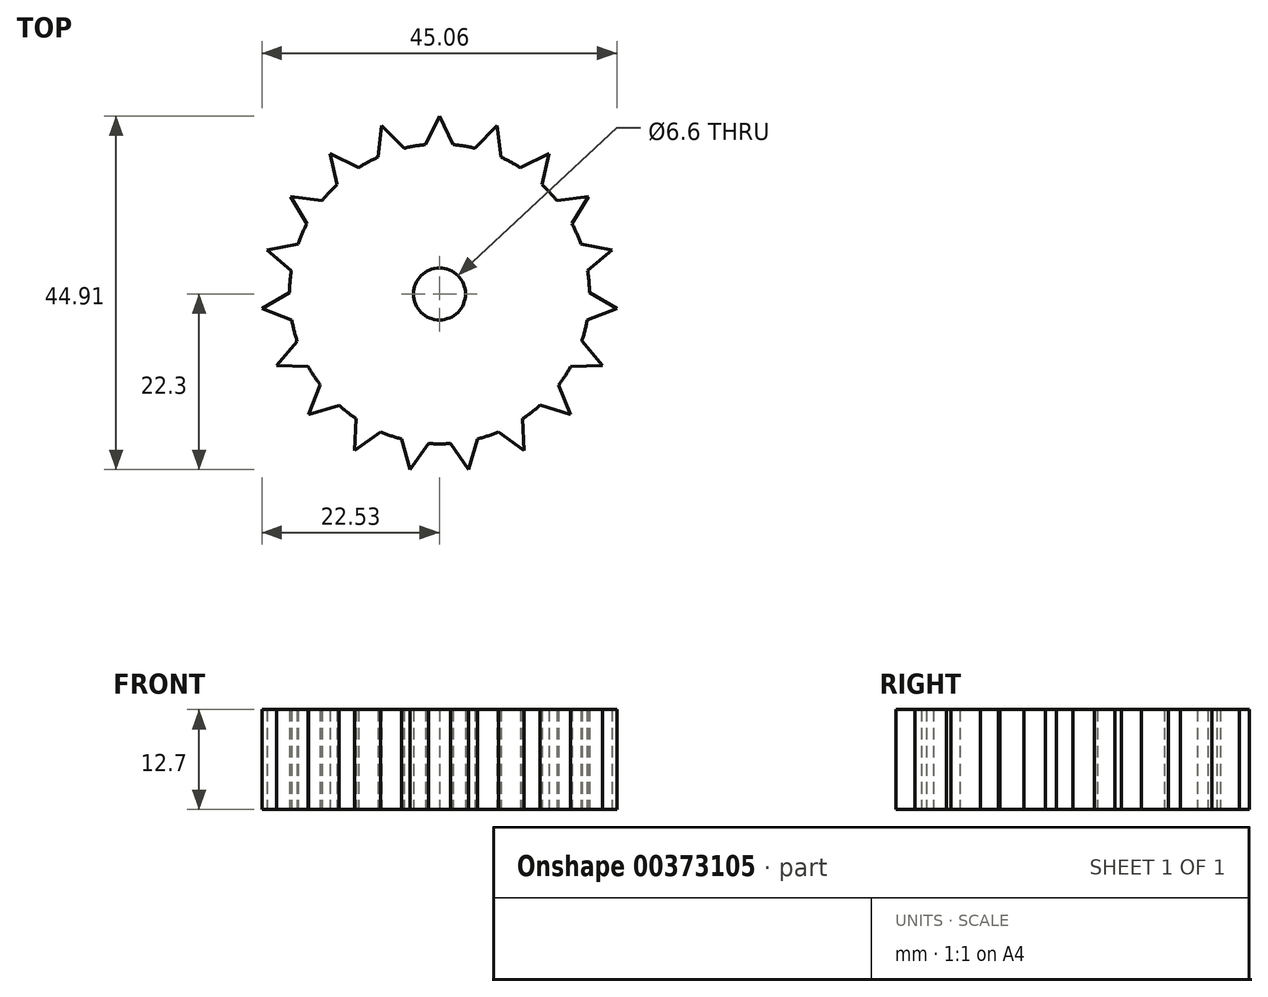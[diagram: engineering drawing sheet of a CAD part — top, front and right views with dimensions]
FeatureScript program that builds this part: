
annotation { "Feature Type Name" : "Feature", "Feature Type Description" : "" }
export const myFeature = defineFeature(function(context is Context, id is Id, definition is map)
    precondition{}
    {
        {
            var Q0;
            Q0=qCreatedBy(makeId("Top.planeOp"),FACE);
            var sketch = newSketch(context, id + "F0", { "sketchPlane" : qUnion([Q0])});
            skCircle(sketch, "E0", {"center": v(0, 0) * mm, "radius": 19.05 * mm});
            skCircle(sketch, "E1", {"center": v(0, 0) * mm, "radius": 3.3 * mm});
            skLineSegment(sketch, "E2", {"start": v(0, 19.05) * mm, "end": v(0, 22.6) * mm});
            skLineSegment(sketch, "E3", {"start": v(0, 22.6) * mm, "end": v(1.75, 18.97) * mm});
            skLineSegment(sketch, "E4", {"start": v(0, 22.6) * mm, "end": v(-1.76, 18.97) * mm});
            skLineSegment(sketch, "E5.1.0", {"start": v(-7.34, 21.38) * mm, "end": v(-4.5, 18.5) * mm});
            skLineSegment(sketch, "E5.1.1", {"start": v(-6.19, 18.02) * mm, "end": v(-7.34, 21.38) * mm});
            skLineSegment(sketch, "E5.1.2", {"start": v(-7.34, 21.38) * mm, "end": v(-7.82, 17.37) * mm});
            skLineSegment(sketch, "E5.2.0", {"start": v(-13.89, 17.84) * mm, "end": v(-10.27, 16.04) * mm});
            skLineSegment(sketch, "E5.2.1", {"start": v(-11.7, 15.03) * mm, "end": v(-13.89, 17.84) * mm});
            skLineSegment(sketch, "E5.2.2", {"start": v(-13.89, 17.84) * mm, "end": v(-13.04, 13.89) * mm});
            skLineSegment(sketch, "E5.3.0", {"start": v(-18.93, 12.36) * mm, "end": v(-14.92, 11.84) * mm});
            skLineSegment(sketch, "E5.3.1", {"start": v(-15.95, 10.42) * mm, "end": v(-18.93, 12.36) * mm});
            skLineSegment(sketch, "E5.3.2", {"start": v(-18.93, 12.36) * mm, "end": v(-16.84, 8.9) * mm});
            skLineSegment(sketch, "E5.4.0", {"start": v(-21.92, 5.55) * mm, "end": v(-17.96, 6.35) * mm});
            skLineSegment(sketch, "E5.4.1", {"start": v(-18.47, 4.68) * mm, "end": v(-21.92, 5.55) * mm});
            skLineSegment(sketch, "E5.4.2", {"start": v(-21.92, 5.55) * mm, "end": v(-18.82, 2.95) * mm});
            skLineSegment(sketch, "E5.5.0", {"start": v(-22.53, -1.87) * mm, "end": v(-19.05, 0.18) * mm});
            skLineSegment(sketch, "E5.5.1", {"start": v(-18.98, -1.57) * mm, "end": v(-22.53, -1.87) * mm});
            skLineSegment(sketch, "E5.5.2", {"start": v(-22.53, -1.87) * mm, "end": v(-18.76, -3.32) * mm});
            skLineSegment(sketch, "E5.6.0", {"start": v(-20.7, -9.08) * mm, "end": v(-18.07, -6.02) * mm});
            skLineSegment(sketch, "E5.6.1", {"start": v(-17.45, -7.65) * mm, "end": v(-20.7, -9.08) * mm});
            skLineSegment(sketch, "E5.6.2", {"start": v(-20.7, -9.08) * mm, "end": v(-16.66, -9.23) * mm});
            skLineSegment(sketch, "E5.7.0", {"start": v(-16.63, -15.31) * mm, "end": v(-15.14, -11.56) * mm});
            skLineSegment(sketch, "E5.7.1", {"start": v(-14.02, -12.9) * mm, "end": v(-16.63, -15.31) * mm});
            skLineSegment(sketch, "E5.7.2", {"start": v(-16.63, -15.31) * mm, "end": v(-12.77, -14.14) * mm});
            skLineSegment(sketch, "E5.8.0", {"start": v(-10.76, -19.88) * mm, "end": v(-10.57, -15.85) * mm});
            skLineSegment(sketch, "E5.8.1", {"start": v(-9.07, -16.75) * mm, "end": v(-10.76, -19.88) * mm});
            skLineSegment(sketch, "E5.8.2", {"start": v(-10.76, -19.88) * mm, "end": v(-7.48, -17.52) * mm});
            skLineSegment(sketch, "E5.9.0", {"start": v(-3.72, -22.3) * mm, "end": v(-4.85, -18.42) * mm});
            skLineSegment(sketch, "E5.9.1", {"start": v(-3.14, -18.8) * mm, "end": v(-3.72, -22.3) * mm});
            skLineSegment(sketch, "E5.9.2", {"start": v(-3.72, -22.3) * mm, "end": v(-1.39, -19) * mm});
            skLineSegment(sketch, "E5.10.0", {"start": v(3.72, -22.3) * mm, "end": v(1.4, -19) * mm});
            skLineSegment(sketch, "E5.10.1", {"start": v(3.14, -18.8) * mm, "end": v(3.72, -22.3) * mm});
            skLineSegment(sketch, "E5.10.2", {"start": v(3.72, -22.3) * mm, "end": v(4.86, -18.42) * mm});
            skLineSegment(sketch, "E5.11.0", {"start": v(10.76, -19.88) * mm, "end": v(7.5, -17.52) * mm});
            skLineSegment(sketch, "E5.11.1", {"start": v(9.07, -16.75) * mm, "end": v(10.76, -19.88) * mm});
            skLineSegment(sketch, "E5.11.2", {"start": v(10.76, -19.88) * mm, "end": v(10.57, -15.85) * mm});
            skLineSegment(sketch, "E5.12.0", {"start": v(16.63, -15.31) * mm, "end": v(12.77, -14.13) * mm});
            skLineSegment(sketch, "E5.12.1", {"start": v(14.02, -12.9) * mm, "end": v(16.63, -15.31) * mm});
            skLineSegment(sketch, "E5.12.2", {"start": v(16.63, -15.31) * mm, "end": v(15.15, -11.55) * mm});
            skLineSegment(sketch, "E5.13.0", {"start": v(20.7, -9.08) * mm, "end": v(16.67, -9.22) * mm});
            skLineSegment(sketch, "E5.13.1", {"start": v(17.45, -7.65) * mm, "end": v(20.7, -9.08) * mm});
            skLineSegment(sketch, "E5.13.2", {"start": v(20.7, -9.08) * mm, "end": v(18.08, -6) * mm});
            skLineSegment(sketch, "E5.14.0", {"start": v(22.53, -1.87) * mm, "end": v(18.76, -3.3) * mm});
            skLineSegment(sketch, "E5.14.1", {"start": v(18.98, -1.57) * mm, "end": v(22.53, -1.87) * mm});
            skLineSegment(sketch, "E5.14.2", {"start": v(22.53, -1.87) * mm, "end": v(19.05, 0.19) * mm});
            skLineSegment(sketch, "E5.15.0", {"start": v(21.92, 5.55) * mm, "end": v(18.82, 2.96) * mm});
            skLineSegment(sketch, "E5.15.1", {"start": v(18.47, 4.68) * mm, "end": v(21.92, 5.55) * mm});
            skLineSegment(sketch, "E5.15.2", {"start": v(21.92, 5.55) * mm, "end": v(17.96, 6.36) * mm});
            skLineSegment(sketch, "E5.16.0", {"start": v(18.93, 12.36) * mm, "end": v(16.84, 8.91) * mm});
            skLineSegment(sketch, "E5.16.1", {"start": v(15.95, 10.42) * mm, "end": v(18.93, 12.36) * mm});
            skLineSegment(sketch, "E5.16.2", {"start": v(18.93, 12.36) * mm, "end": v(14.92, 11.85) * mm});
            skLineSegment(sketch, "E5.17.0", {"start": v(13.89, 17.84) * mm, "end": v(13.03, 13.9) * mm});
            skLineSegment(sketch, "E5.17.1", {"start": v(11.7, 15.03) * mm, "end": v(13.89, 17.84) * mm});
            skLineSegment(sketch, "E5.17.2", {"start": v(13.89, 17.84) * mm, "end": v(10.26, 16.05) * mm});
            skLineSegment(sketch, "E5.18.0", {"start": v(7.34, 21.38) * mm, "end": v(7.81, 17.37) * mm});
            skLineSegment(sketch, "E5.18.1", {"start": v(6.19, 18.02) * mm, "end": v(7.34, 21.38) * mm});
            skLineSegment(sketch, "E5.18.2", {"start": v(7.34, 21.38) * mm, "end": v(4.5, 18.51) * mm});
            skSolve(sketch);
        }
        {
            var Q0;
            {var subQ0=sQuery(id+"F0.wireOp",EDGE,"E5.13.0");Q0=makeQuery(id+"F0.imprint","IMPRINT",FACE,{"disambiguationData":[TD([[makeQuery(id+"F0.imprint","IMPRINT",EDGE,{"derivedFrom":subQ0}),-1.0]])]});}
            var Q1;
            {var subQ0=sQuery(id+"F0.wireOp",EDGE,"E5.5.0");Q1=makeQuery(id+"F0.imprint","IMPRINT",FACE,{"disambiguationData":[TD([[makeQuery(id+"F0.imprint","IMPRINT",EDGE,{"derivedFrom":subQ0}),-1.0]])]});}
            var Q2;
            {var subQ0=sQuery(id+"F0.wireOp",EDGE,"E5.5.1");Q2=makeQuery(id+"F0.imprint","IMPRINT",FACE,{"disambiguationData":[TD([[makeQuery(id+"F0.imprint","IMPRINT",EDGE,{"derivedFrom":subQ0}),1.0]])]});}
            var Q3;
            {var subQ0=sQuery(id+"F0.wireOp",EDGE,"E5.10.0");Q3=makeQuery(id+"F0.imprint","IMPRINT",FACE,{"disambiguationData":[TD([[makeQuery(id+"F0.imprint","IMPRINT",EDGE,{"derivedFrom":subQ0}),-1.0]])]});}
            var Q4;
            {var subQ0=sQuery(id+"F0.wireOp",EDGE,"E5.13.1");Q4=makeQuery(id+"F0.imprint","IMPRINT",FACE,{"disambiguationData":[TD([[makeQuery(id+"F0.imprint","IMPRINT",EDGE,{"derivedFrom":subQ0}),1.0]])]});}
            var Q5;
            {var subQ0=sQuery(id+"F0.wireOp",EDGE,"E5.9.0");Q5=makeQuery(id+"F0.imprint","IMPRINT",FACE,{"disambiguationData":[TD([[makeQuery(id+"F0.imprint","IMPRINT",EDGE,{"derivedFrom":subQ0}),-1.0]])]});}
            var Q6;
            {var subQ0=sQuery(id+"F0.wireOp",EDGE,"E5.6.0");Q6=makeQuery(id+"F0.imprint","IMPRINT",FACE,{"disambiguationData":[TD([[makeQuery(id+"F0.imprint","IMPRINT",EDGE,{"derivedFrom":subQ0}),-1.0]])]});}
            var Q7;
            {var subQ0=sQuery(id+"F0.wireOp",EDGE,"E5.14.0");Q7=makeQuery(id+"F0.imprint","IMPRINT",FACE,{"disambiguationData":[TD([[makeQuery(id+"F0.imprint","IMPRINT",EDGE,{"derivedFrom":subQ0}),-1.0]])]});}
            var Q8;
            {var subQ0=sQuery(id+"F0.wireOp",EDGE,"E5.10.1");Q8=makeQuery(id+"F0.imprint","IMPRINT",FACE,{"disambiguationData":[TD([[makeQuery(id+"F0.imprint","IMPRINT",EDGE,{"derivedFrom":subQ0}),1.0]])]});}
            var Q9;
            {var subQ0=sQuery(id+"F0.wireOp",EDGE,"E5.9.1");Q9=makeQuery(id+"F0.imprint","IMPRINT",FACE,{"disambiguationData":[TD([[makeQuery(id+"F0.imprint","IMPRINT",EDGE,{"derivedFrom":subQ0}),1.0]])]});}
            var Q10;
            {var subQ0=sQuery(id+"F0.wireOp",EDGE,"E5.14.1");Q10=makeQuery(id+"F0.imprint","IMPRINT",FACE,{"disambiguationData":[TD([[makeQuery(id+"F0.imprint","IMPRINT",EDGE,{"derivedFrom":subQ0}),1.0]])]});}
            var Q11;
            {var subQ0=sQuery(id+"F0.wireOp",EDGE,"E5.6.1");Q11=makeQuery(id+"F0.imprint","IMPRINT",FACE,{"disambiguationData":[TD([[makeQuery(id+"F0.imprint","IMPRINT",EDGE,{"derivedFrom":subQ0}),1.0]])]});}
            var Q12;
            {var subQ0=sQuery(id+"F0.wireOp",EDGE,"E5.3.0");Q12=makeQuery(id+"F0.imprint","IMPRINT",FACE,{"disambiguationData":[TD([[makeQuery(id+"F0.imprint","IMPRINT",EDGE,{"derivedFrom":subQ0}),-1.0]])]});}
            var Q13;
            {var subQ0=sQuery(id+"F0.wireOp",EDGE,"E5.2.0");Q13=makeQuery(id+"F0.imprint","IMPRINT",FACE,{"disambiguationData":[TD([[makeQuery(id+"F0.imprint","IMPRINT",EDGE,{"derivedFrom":subQ0}),-1.0]])]});}
            var Q14;
            {var subQ0=sQuery(id+"F0.wireOp",EDGE,"E5.3.1");Q14=makeQuery(id+"F0.imprint","IMPRINT",FACE,{"disambiguationData":[TD([[makeQuery(id+"F0.imprint","IMPRINT",EDGE,{"derivedFrom":subQ0}),1.0]])]});}
            var Q15;
            {var subQ0=sQuery(id+"F0.wireOp",EDGE,"E5.2.1");Q15=makeQuery(id+"F0.imprint","IMPRINT",FACE,{"disambiguationData":[TD([[makeQuery(id+"F0.imprint","IMPRINT",EDGE,{"derivedFrom":subQ0}),1.0]])]});}
            var Q16;
            {var subQ0=sQuery(id+"F0.wireOp",EDGE,"E5.15.0");Q16=makeQuery(id+"F0.imprint","IMPRINT",FACE,{"disambiguationData":[TD([[makeQuery(id+"F0.imprint","IMPRINT",EDGE,{"derivedFrom":subQ0}),-1.0]])]});}
            var Q17;
            {var subQ0=sQuery(id+"F0.wireOp",EDGE,"E5.15.1");Q17=makeQuery(id+"F0.imprint","IMPRINT",FACE,{"disambiguationData":[TD([[makeQuery(id+"F0.imprint","IMPRINT",EDGE,{"derivedFrom":subQ0}),1.0]])]});}
            var Q18;
            {var subQ0=sQuery(id+"F0.wireOp",EDGE,"E5.16.0");Q18=makeQuery(id+"F0.imprint","IMPRINT",FACE,{"disambiguationData":[TD([[makeQuery(id+"F0.imprint","IMPRINT",EDGE,{"derivedFrom":subQ0}),-1.0]])]});}
            var Q19;
            {var subQ0=sQuery(id+"F0.wireOp",EDGE,"E5.16.1");Q19=makeQuery(id+"F0.imprint","IMPRINT",FACE,{"disambiguationData":[TD([[makeQuery(id+"F0.imprint","IMPRINT",EDGE,{"derivedFrom":subQ0}),1.0]])]});}
            var Q20;
            {var subQ0=sQuery(id+"F0.wireOp",EDGE,"E5.17.0");Q20=makeQuery(id+"F0.imprint","IMPRINT",FACE,{"disambiguationData":[TD([[makeQuery(id+"F0.imprint","IMPRINT",EDGE,{"derivedFrom":subQ0}),-1.0]])]});}
            var Q21;
            {var subQ0=sQuery(id+"F0.wireOp",EDGE,"E5.17.1");Q21=makeQuery(id+"F0.imprint","IMPRINT",FACE,{"disambiguationData":[TD([[makeQuery(id+"F0.imprint","IMPRINT",EDGE,{"derivedFrom":subQ0}),1.0]])]});}
            var Q22;
            {var subQ0=sQuery(id+"F0.wireOp",EDGE,"E5.18.0");Q22=makeQuery(id+"F0.imprint","IMPRINT",FACE,{"disambiguationData":[TD([[makeQuery(id+"F0.imprint","IMPRINT",EDGE,{"derivedFrom":subQ0}),-1.0]])]});}
            var Q23;
            {var subQ0=sQuery(id+"F0.wireOp",EDGE,"E5.18.1");Q23=makeQuery(id+"F0.imprint","IMPRINT",FACE,{"disambiguationData":[TD([[makeQuery(id+"F0.imprint","IMPRINT",EDGE,{"derivedFrom":subQ0}),1.0]])]});}
            var Q24;
            {var subQ0=sQuery(id+"F0.wireOp",EDGE,"E2");Q24=makeQuery(id+"F0.imprint","IMPRINT",FACE,{"disambiguationData":[TD([[makeQuery(id+"F0.imprint","IMPRINT",EDGE,{"derivedFrom":subQ0}),-1.0]])]});}
            var Q25;
            {var subQ0=sQuery(id+"F0.wireOp",EDGE,"E2");Q25=makeQuery(id+"F0.imprint","IMPRINT",FACE,{"disambiguationData":[TD([[makeQuery(id+"F0.imprint","IMPRINT",EDGE,{"derivedFrom":subQ0}),1.0]])]});}
            var Q26;
            {var subQ0=sQuery(id+"F0.wireOp",EDGE,"E5.1.0");Q26=makeQuery(id+"F0.imprint","IMPRINT",FACE,{"disambiguationData":[TD([[makeQuery(id+"F0.imprint","IMPRINT",EDGE,{"derivedFrom":subQ0}),-1.0]])]});}
            var Q27;
            {var subQ0=sQuery(id+"F0.wireOp",EDGE,"E5.1.1");Q27=makeQuery(id+"F0.imprint","IMPRINT",FACE,{"disambiguationData":[TD([[makeQuery(id+"F0.imprint","IMPRINT",EDGE,{"derivedFrom":subQ0}),1.0]])]});}
            var Q28;
            {var subQ0=sQuery(id+"F0.wireOp",EDGE,"E5.7.0");Q28=makeQuery(id+"F0.imprint","IMPRINT",FACE,{"disambiguationData":[TD([[makeQuery(id+"F0.imprint","IMPRINT",EDGE,{"derivedFrom":subQ0}),-1.0]])]});}
            var Q29;
            {var subQ0=sQuery(id+"F0.wireOp",EDGE,"E5.4.0");Q29=makeQuery(id+"F0.imprint","IMPRINT",FACE,{"disambiguationData":[TD([[makeQuery(id+"F0.imprint","IMPRINT",EDGE,{"derivedFrom":subQ0}),-1.0]])]});}
            var Q30;
            {var subQ0=sQuery(id+"F0.wireOp",EDGE,"E5.12.0");Q30=makeQuery(id+"F0.imprint","IMPRINT",FACE,{"disambiguationData":[TD([[makeQuery(id+"F0.imprint","IMPRINT",EDGE,{"derivedFrom":subQ0}),-1.0]])]});}
            var Q31;
            {var subQ0=sQuery(id+"F0.wireOp",EDGE,"E5.7.1");Q31=makeQuery(id+"F0.imprint","IMPRINT",FACE,{"disambiguationData":[TD([[makeQuery(id+"F0.imprint","IMPRINT",EDGE,{"derivedFrom":subQ0}),1.0]])]});}
            var Q32;
            {var subQ0=sQuery(id+"F0.wireOp",EDGE,"E5.4.1");Q32=makeQuery(id+"F0.imprint","IMPRINT",FACE,{"disambiguationData":[TD([[makeQuery(id+"F0.imprint","IMPRINT",EDGE,{"derivedFrom":subQ0}),1.0]])]});}
            var Q33;
            {var subQ0=sQuery(id+"F0.wireOp",EDGE,"E5.12.1");Q33=makeQuery(id+"F0.imprint","IMPRINT",FACE,{"disambiguationData":[TD([[makeQuery(id+"F0.imprint","IMPRINT",EDGE,{"derivedFrom":subQ0}),1.0]])]});}
            var Q34;
            Q34=makeQuery(id+"F0.imprint","IMPRINT",FACE,{"disambiguationData":[TD([[makeQuery(id+"F0.imprint","IMPRINT",EDGE,{"derivedFrom":sQuery(id+"F0.wireOp",EDGE,"E1")}),-1.0]])]});
            var Q35;
            {var subQ0=sQuery(id+"F0.wireOp",EDGE,"E5.8.1");Q35=makeQuery(id+"F0.imprint","IMPRINT",FACE,{"disambiguationData":[TD([[makeQuery(id+"F0.imprint","IMPRINT",EDGE,{"derivedFrom":subQ0}),1.0]])]});}
            var Q36;
            {var subQ0=sQuery(id+"F0.wireOp",EDGE,"E5.8.0");Q36=makeQuery(id+"F0.imprint","IMPRINT",FACE,{"disambiguationData":[TD([[makeQuery(id+"F0.imprint","IMPRINT",EDGE,{"derivedFrom":subQ0}),-1.0]])]});}
            var Q37;
            {var subQ0=sQuery(id+"F0.wireOp",EDGE,"E5.11.1");Q37=makeQuery(id+"F0.imprint","IMPRINT",FACE,{"disambiguationData":[TD([[makeQuery(id+"F0.imprint","IMPRINT",EDGE,{"derivedFrom":subQ0}),1.0]])]});}
            var Q38;
            {var subQ0=sQuery(id+"F0.wireOp",EDGE,"E5.11.0");Q38=makeQuery(id+"F0.imprint","IMPRINT",FACE,{"disambiguationData":[TD([[makeQuery(id+"F0.imprint","IMPRINT",EDGE,{"derivedFrom":subQ0}),-1.0]])]});}
            extrude(context, id + "F1", {"entities" : qUnion([Q0, Q1, Q2, Q3, Q4, Q5, Q6, Q7, Q8, Q9, Q10, Q11, Q12, Q13, Q14, Q15, Q16, Q17, Q18, Q19, Q20, Q21, Q22, Q23, Q24, Q25, Q26, Q27, Q28, Q29, Q30, Q31, Q32, Q33, Q34, Q35, Q36, Q37, Q38]), "depth" : 12.7 * mm});
        }
    });
